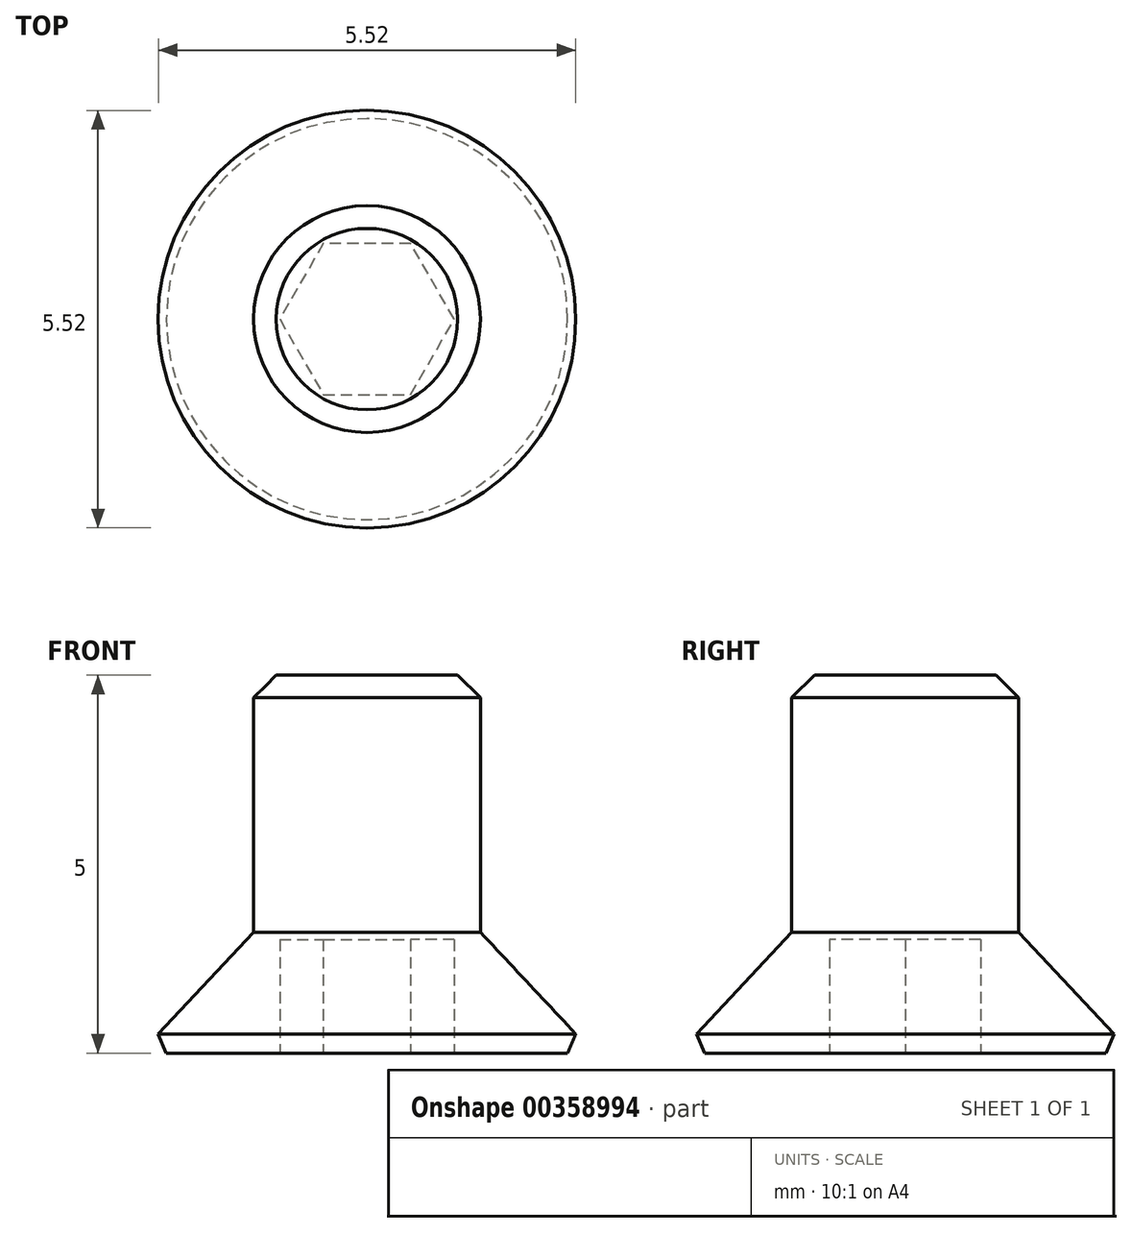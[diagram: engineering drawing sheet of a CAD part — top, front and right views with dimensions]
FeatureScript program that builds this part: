
annotation { "Feature Type Name" : "Feature", "Feature Type Description" : "" }
export const myFeature = defineFeature(function(context is Context, id is Id, definition is map)
    precondition{}
    {
        {
            assignVariable(context, id + "F0", {"name" : "d", "anyValue" : 3});
        }
        {
            var Q0;
            Q0=qCreatedBy(makeId("Front.planeOp"),FACE);
            var sketch = newSketch(context, id + "F1", { "sketchPlane" : qUnion([Q0])});
            skLineSegment(sketch, "E0", {"start": v(0, 0) * mm, "end": v(3, 0) * mm});
            skLineSegment(sketch, "E1", {"start": v(3, 0) * mm, "end": v(1.5, 1.6) * mm});
            skLineSegment(sketch, "E2", {"start": v(1.5, 1.6) * mm, "end": v(1.5, 5) * mm});
            skLineSegment(sketch, "E3", {"start": v(1.5, 5) * mm, "end": v(0, 5) * mm});
            skLineSegment(sketch, "E4", {"start": v(0, 5) * mm, "end": v(0, 0) * mm});
            skSolve(sketch);
        }
        {
            var Q0;
            Q0=qSketchRegion(id+"F1",true);
            var Q1;
            Q1=sQuery(id+"F1.wireOp",EDGE,"E4");
            revolve(context, id + "F2", {"entities" : qUnion([Q0]), "axis" : qUnion([Q1]), "revolveType" : RevolveType.FULL});
        }
        {
            var Q0;
            Q0=makeQuery(id+"F2.opRevolve","SWEPT_FACE",FACE,{"disambiguationData":[OSD([sQuery(id+"F1.wireOp",EDGE,"E0")])]});
            var sketch = newSketch(context, id + "F3", { "sketchPlane" : qUnion([Q0])});
            skCircle(sketch, "E5.cCircle", {"center": v(0, 0) * mm, "radius": 1 * mm, "construction": true});
            skLineSegment(sketch, "E5.0", {"start": v(-0.58, 1) * mm, "end": v(0.58, 1) * mm});
            skLineSegment(sketch, "E5.1", {"start": v(0.58, 1) * mm, "end": v(1.15, 0) * mm});
            skLineSegment(sketch, "E5.2", {"start": v(1.15, 0) * mm, "end": v(0.58, -1) * mm});
            skLineSegment(sketch, "E5.3", {"start": v(0.58, -1) * mm, "end": v(-0.58, -1) * mm});
            skLineSegment(sketch, "E5.4", {"start": v(-0.58, -1) * mm, "end": v(-1.15, 0) * mm});
            skLineSegment(sketch, "E5.5", {"start": v(-1.15, 0) * mm, "end": v(-0.58, 1) * mm});
            skPoint(sketch, "E5.0.midPoint", {"position": v(0, 1) * mm});
            skSolve(sketch);
        }
        {
            var Q0;
            Q0=qSketchRegion(id+"F3",true);
            extrude(context, id + "F4", {"entities" : qUnion([Q0]), "operationType" : NewBodyOperationType.REMOVE, "oppositeDirection" : true, "depth" : (getVariable(context, 'd') / 2) * mm});
        }
        {
            var Q0;
            Q0=makeQuery(id+"F2.opRevolve","SWEPT_EDGE",EDGE,{"disambiguationData":[OSD([sQuery(id+"F1.wireOp",EDGE,"E0"),sQuery(id+"F1.wireOp",EDGE,"E1")])]});
            var Q1;
            Q1=makeQuery(id+"F4.boolean.opBoolean","COPY",EDGE,{"derivedFrom":makeQuery(id+"F4.opExtrude","CAP_EDGE",EDGE,{"disambiguationData":[OSD([sQuery(id+"F3.wireOp",EDGE,"E5.0")])],"isStart":true})});
            var Q2;
            Q2=makeQuery(id+"F4.boolean.opBoolean","COPY",EDGE,{"derivedFrom":makeQuery(id+"F4.opExtrude","CAP_EDGE",EDGE,{"disambiguationData":[OSD([sQuery(id+"F3.wireOp",EDGE,"E5.5")])],"isStart":true})});
            var Q3;
            Q3=makeQuery(id+"F4.boolean.opBoolean","COPY",EDGE,{"derivedFrom":makeQuery(id+"F4.opExtrude","CAP_EDGE",EDGE,{"disambiguationData":[OSD([sQuery(id+"F3.wireOp",EDGE,"E5.4")])],"isStart":true})});
            var Q4;
            Q4=makeQuery(id+"F4.boolean.opBoolean","COPY",EDGE,{"derivedFrom":makeQuery(id+"F4.opExtrude","CAP_EDGE",EDGE,{"disambiguationData":[OSD([sQuery(id+"F3.wireOp",EDGE,"E5.3")])],"isStart":true})});
            var Q5;
            Q5=makeQuery(id+"F4.boolean.opBoolean","COPY",EDGE,{"derivedFrom":makeQuery(id+"F4.opExtrude","CAP_EDGE",EDGE,{"disambiguationData":[OSD([sQuery(id+"F3.wireOp",EDGE,"E5.2")])],"isStart":true})});
            var Q6;
            Q6=makeQuery(id+"F4.boolean.opBoolean","COPY",EDGE,{"derivedFrom":makeQuery(id+"F4.opExtrude","CAP_EDGE",EDGE,{"disambiguationData":[OSD([sQuery(id+"F3.wireOp",EDGE,"E5.1")])],"isStart":true})});
            chamfer(context, id + "F5", {"entities" : qUnion([Q0, Q1, Q2, Q3, Q4, Q5, Q6]), "width" : (getVariable(context, 'd') / 20) * mm, "tangentPropagation" : true});
        }
        {
            var Q0;
            Q0=makeQuery(id+"F2.opRevolve","SWEPT_EDGE",EDGE,{"disambiguationData":[OSD([sQuery(id+"F1.wireOp",EDGE,"E2"),sQuery(id+"F1.wireOp",EDGE,"E3")])]});
            chamfer(context, id + "F6", {"entities" : qUnion([Q0]), "width" : (getVariable(context, 'd') / 10) * mm, "tangentPropagation" : true});
        }
    });
